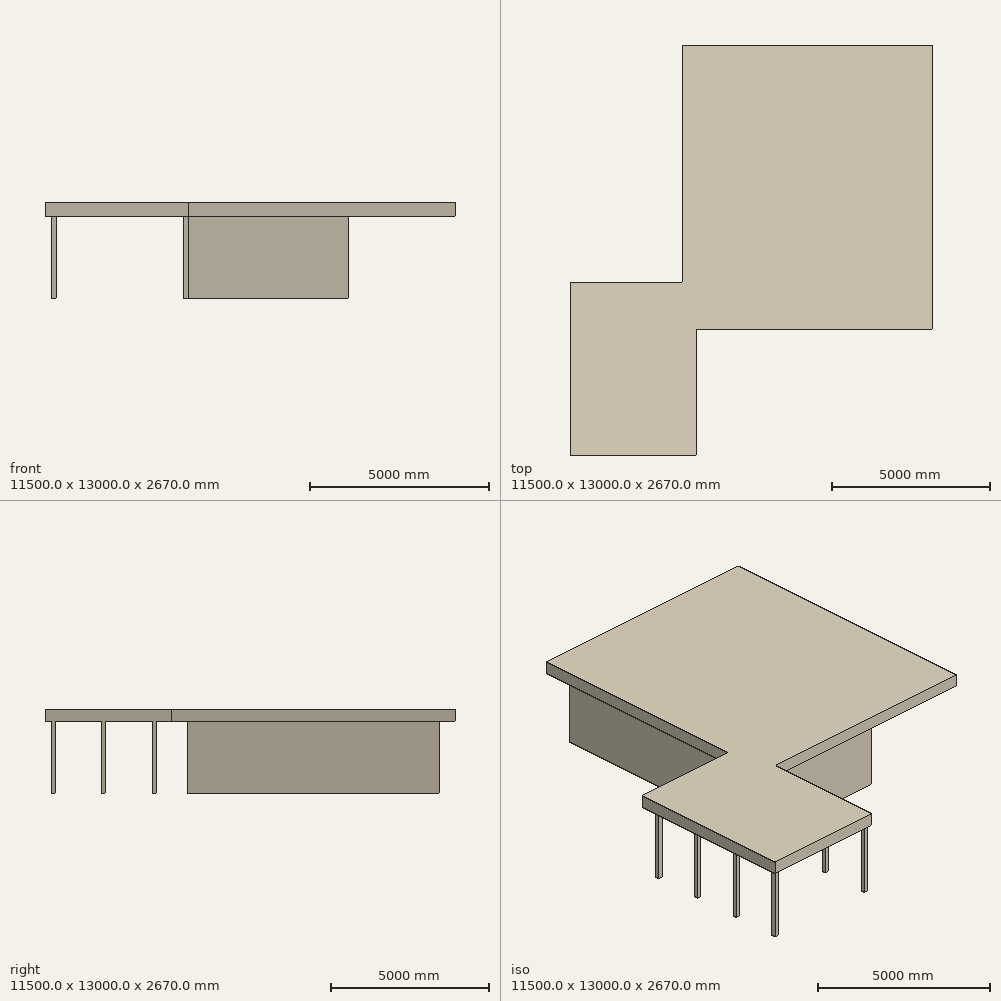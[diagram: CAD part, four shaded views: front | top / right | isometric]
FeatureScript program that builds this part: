
annotation { "Feature Type Name" : "Feature", "Feature Type Description" : "" }
export const myFeature = defineFeature(function(context is Context, id is Id, definition is map)
    precondition{}
    {
        {
            var Q0;
            Q0=qCreatedBy(makeId("Top.planeOp"),FACE);
            var sketch = newSketch(context, id + "F0", { "sketchPlane" : qUnion([Q0])});
            skLineSegment(sketch, "E0", {"start": v(0, 0) * mm, "end": v(7500, 0) * mm});
            skLineSegment(sketch, "E1", {"start": v(0, 0) * mm, "end": v(0, -4000) * mm});
            skLineSegment(sketch, "E2", {"start": v(0, -4000) * mm, "end": v(-4000, -4000) * mm});
            skLineSegment(sketch, "E3", {"start": v(-4000, -4000) * mm, "end": v(-4000, 1500) * mm});
            skLineSegment(sketch, "E4", {"start": v(-450, 9000) * mm, "end": v(7500, 9000) * mm});
            skLineSegment(sketch, "E5", {"start": v(7500, 9000) * mm, "end": v(7500, 0) * mm});
            skLineSegment(sketch, "E6", {"start": v(-4000, 1500) * mm, "end": v(-450, 1500) * mm});
            skLineSegment(sketch, "E7", {"start": v(-450, 9000) * mm, "end": v(-450, 1500) * mm});
            skSolve(sketch);
        }
        {
            var Q0;
            Q0 = qSketchRegion(id + "F0", true);
            extrude(context, id + "F1", {"entities" : qUnion([Q0]), "depth" : 380 * mm, "offsetDistance" : 25 * mm});
        }
        {
            var Q0;
            Q0=makeQuery(id+"F1.opExtrude","CAP_FACE",FACE,{"disambiguationData":[OSD([sQuery(id+"F0.wireOp",EDGE,"E0"),sQuery(id+"F0.wireOp",EDGE,"E1"),sQuery(id+"F0.wireOp",EDGE,"E2"),sQuery(id+"F0.wireOp",EDGE,"E3"),sQuery(id+"F0.wireOp",EDGE,"Vto1C8C6-i7Z3-1Jsl-U6Hy-glV7F70Au2TP"),sQuery(id+"F0.wireOp",EDGE,"picyocfe-7ov7-HRw2-SZbi-OqdjEEkKBgfg"),sQuery(id+"F0.wireOp",EDGE,"E4"),sQuery(id+"F0.wireOp",EDGE,"E5")])],"isStart":true});
            var sketch = newSketch(context, id + "F2", { "sketchPlane" : qUnion([Q0])});
            skLineSegment(sketch, "E8.bottom", {"start": v(-3820, 3820) * mm, "end": v(-3690, 3820) * mm});
            skLineSegment(sketch, "E8.top", {"start": v(-3820, 3690) * mm, "end": v(-3690, 3690) * mm});
            skLineSegment(sketch, "E8.left", {"start": v(-3820, 3820) * mm, "end": v(-3820, 3690) * mm});
            skLineSegment(sketch, "E8.right", {"start": v(-3690, 3820) * mm, "end": v(-3690, 3690) * mm});
            skLineSegment(sketch, "E9.0.1.0", {"start": v(-3820, 2220) * mm, "end": v(-3820, 2090) * mm});
            skLineSegment(sketch, "E9.0.1.1", {"start": v(-3820, 2220) * mm, "end": v(-3690, 2220) * mm});
            skLineSegment(sketch, "E9.0.1.2", {"start": v(-3820, 2090) * mm, "end": v(-3690, 2090) * mm});
            skLineSegment(sketch, "E9.0.1.3", {"start": v(-3690, 2220) * mm, "end": v(-3690, 2090) * mm});
            skLineSegment(sketch, "E9.1.0.0", {"start": v(-130, 3820) * mm, "end": v(-130, 3690) * mm});
            skLineSegment(sketch, "E9.1.0.1", {"start": v(-130, 3820) * mm, "end": v(0, 3820) * mm});
            skLineSegment(sketch, "E9.1.0.2", {"start": v(-130, 3690) * mm, "end": v(0, 3690) * mm});
            skLineSegment(sketch, "E9.1.0.3", {"start": v(0, 3820) * mm, "end": v(0, 3690) * mm});
            skLineSegment(sketch, "E9.1.1.0", {"start": v(-130, 2220) * mm, "end": v(-130, 2090) * mm});
            skLineSegment(sketch, "E9.1.1.1", {"start": v(-130, 2220) * mm, "end": v(0, 2220) * mm});
            skLineSegment(sketch, "E9.1.1.2", {"start": v(-130, 2090) * mm, "end": v(0, 2090) * mm});
            skLineSegment(sketch, "E9.1.1.3", {"start": v(0, 2220) * mm, "end": v(0, 2090) * mm});
            skLineSegment(sketch, "E9.direction1", {"start": v(-3820, 3690) * mm, "end": v(-130, 3690) * mm, "construction": true});
            skLineSegment(sketch, "E9.direction2", {"start": v(-3820, 3690) * mm, "end": v(-3820, 2090) * mm, "construction": true});
            skLineSegment(sketch, "E10.0.0.2", {"start": v(-3820, 620) * mm, "end": v(-3820, 490) * mm});
            skLineSegment(sketch, "E10.3.0.2", {"start": v(-3820, 620) * mm, "end": v(-3690, 620) * mm});
            skLineSegment(sketch, "E10.6.0.2", {"start": v(-3820, 490) * mm, "end": v(-3690, 490) * mm});
            skLineSegment(sketch, "E10.9.0.2", {"start": v(-3690, 620) * mm, "end": v(-3690, 490) * mm});
            skLineSegment(sketch, "E10.0.0.3", {"start": v(-3820, -980) * mm, "end": v(-3820, -1110) * mm});
            skLineSegment(sketch, "E10.3.0.3", {"start": v(-3820, -980) * mm, "end": v(-3690, -980) * mm});
            skLineSegment(sketch, "E10.6.0.3", {"start": v(-3820, -1110) * mm, "end": v(-3690, -1110) * mm});
            skLineSegment(sketch, "E10.9.0.3", {"start": v(-3690, -980) * mm, "end": v(-3690, -1110) * mm});
            skLineSegment(sketch, "E10.0.1.2", {"start": v(-130, 620) * mm, "end": v(-130, 490) * mm});
            skLineSegment(sketch, "E10.3.1.2", {"start": v(-130, 620) * mm, "end": v(0, 620) * mm});
            skLineSegment(sketch, "E10.6.1.2", {"start": v(-130, 490) * mm, "end": v(0, 490) * mm});
            skLineSegment(sketch, "E10.9.1.2", {"start": v(0, 620) * mm, "end": v(0, 490) * mm});
            skLineSegment(sketch, "E10.0.1.3", {"start": v(-130, -980) * mm, "end": v(-130, -1110) * mm});
            skLineSegment(sketch, "E10.3.1.3", {"start": v(-130, -980) * mm, "end": v(0, -980) * mm});
            skLineSegment(sketch, "E10.6.1.3", {"start": v(-130, -1110) * mm, "end": v(0, -1110) * mm});
            skLineSegment(sketch, "E10.9.1.3", {"start": v(0, -980) * mm, "end": v(0, -1110) * mm});
            skSolve(sketch);
        }
        {
            var Q0;
            Q0 = qSketchRegion(id + "F2", true);
            extrude(context, id + "F3", {"entities" : qUnion([Q0]), "operationType" : NewBodyOperationType.ADD, "depth" : 2290 * mm, "offsetDistance" : 25 * mm});
        }
        {
            var Q0;
            Q0=makeQuery(id+"F1.opExtrude","CAP_FACE",FACE,{"disambiguationData":[OSD([sQuery(id+"F0.wireOp",EDGE,"E0"),sQuery(id+"F0.wireOp",EDGE,"E1"),sQuery(id+"F0.wireOp",EDGE,"E2"),sQuery(id+"F0.wireOp",EDGE,"E3"),sQuery(id+"F0.wireOp",EDGE,"E4"),sQuery(id+"F0.wireOp",EDGE,"E5"),sQuery(id+"F0.wireOp",EDGE,"E6"),sQuery(id+"F0.wireOp",EDGE,"E7")])],"isStart":true});
            var sketch = newSketch(context, id + "F4", { "sketchPlane" : qUnion([Q0])});
            skLineSegment(sketch, "E11.bottom", {"start": v(0, -500) * mm, "end": v(4500, -500) * mm});
            skLineSegment(sketch, "E11.top", {"start": v(0, -8500) * mm, "end": v(4500, -8500) * mm});
            skLineSegment(sketch, "E11.left", {"start": v(0, -500) * mm, "end": v(0, -8500) * mm});
            skLineSegment(sketch, "E11.right", {"start": v(4500, -500) * mm, "end": v(4500, -8500) * mm});
            skSolve(sketch);
        }
        {
            var Q0;
            Q0 = qSketchRegion(id + "F4", true);
            extrude(context, id + "F5", {"entities" : qUnion([Q0]), "operationType" : NewBodyOperationType.ADD, "depth" : 2290 * mm, "offsetDistance" : 25 * mm});
        }
    });
